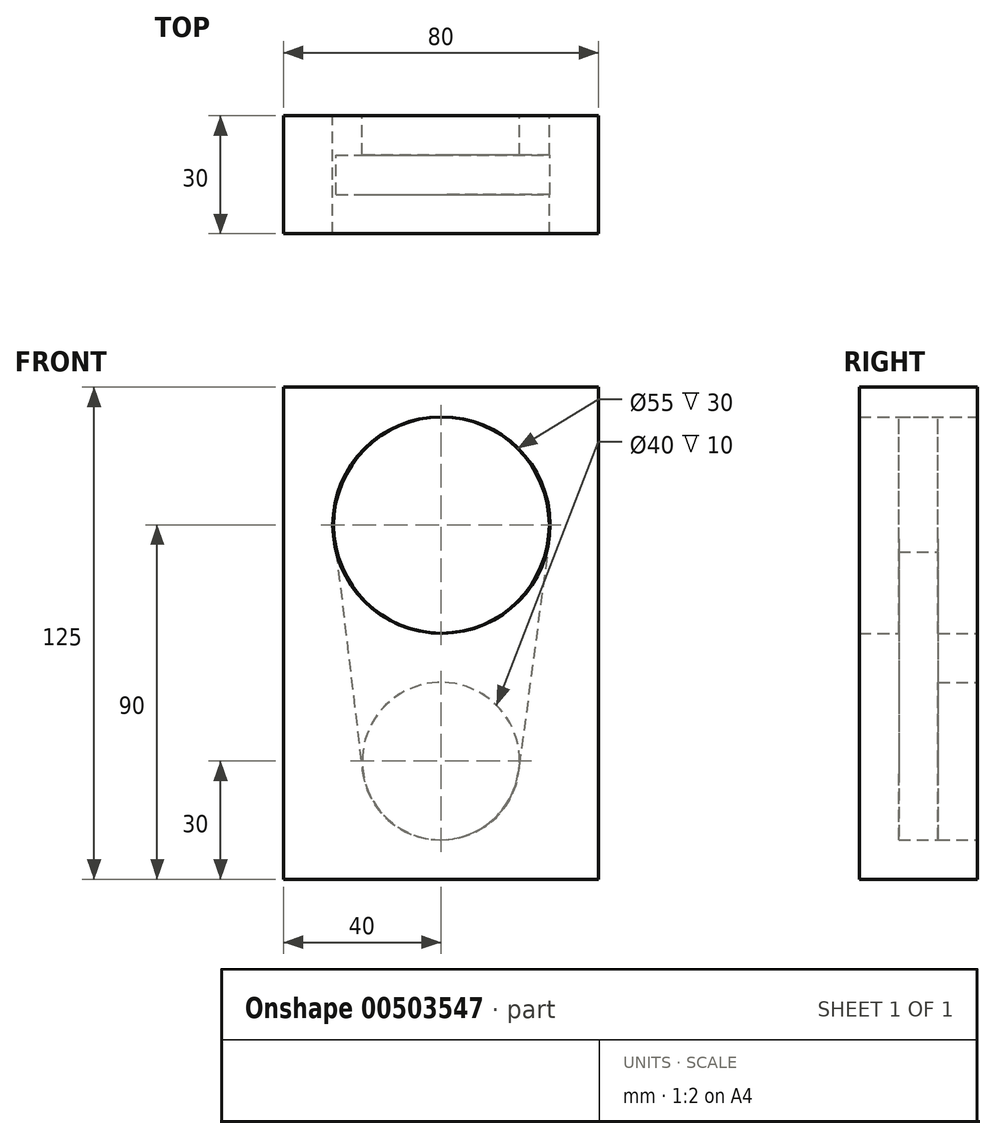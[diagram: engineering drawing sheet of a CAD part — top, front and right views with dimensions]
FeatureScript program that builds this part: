
annotation { "Feature Type Name" : "Feature", "Feature Type Description" : "" }
export const myFeature = defineFeature(function(context is Context, id is Id, definition is map)
    precondition{}
    {
        {
            var Q0;
            Q0=qCreatedBy(makeId("Front.planeOp"),FACE);
            var sketch = newSketch(context, id + "F0", { "sketchPlane" : qUnion([Q0])});
            skLineSegment(sketch, "E0", {"start": v(-27.07, 36.74) * mm, "end": v(-20, -22.37) * mm});
            skLineSegment(sketch, "E1", {"start": v(27.5, 36.4) * mm, "end": v(19.69, -22.63) * mm});
            skArc(sketch, "E2", {"start": v(-20, -22.37) * mm, "mid": v(-0.27, -40) * mm, "end": v(19.69, -22.63) * mm});
            skArc(sketch, "E3", {"start": v(27.5, 36.4) * mm, "mid": v(0.41, 67.5) * mm, "end": v(-27.07, 36.74) * mm});
            skSolve(sketch);
        }
        {
            var Q0;
            Q0=qCreatedBy(makeId("Front.planeOp"),FACE);
            var sketch = newSketch(context, id + "F1", { "sketchPlane" : qUnion([Q0])});
            skCircle(sketch, "E4", {"center": v(0, -20) * mm, "radius": 20 * mm});
            skSolve(sketch);
        }
        {
            var Q0;
            Q0=qCreatedBy(makeId("Front.planeOp"),FACE);
            var sketch = newSketch(context, id + "F2", { "sketchPlane" : qUnion([Q0])});
            skLineSegment(sketch, "E5.bottom", {"start": v(-40, 75) * mm, "end": v(40, 75) * mm});
            skLineSegment(sketch, "E5.top", {"start": v(-40, -50) * mm, "end": v(40, -50) * mm});
            skLineSegment(sketch, "E5.left", {"start": v(-40, 75) * mm, "end": v(-40, -50) * mm});
            skLineSegment(sketch, "E5.right", {"start": v(40, 75) * mm, "end": v(40, -50) * mm});
            skCircle(sketch, "E6", {"center": v(0, 40) * mm, "radius": 27.5 * mm});
            skSolve(sketch);
        }
        {
            var Q0;
            Q0 = qSketchRegion(id + "F2", true);
            extrude(context, id + "F3", {"entities" : qUnion([Q0]), "depth" : 30 * mm});
        }
        {
            var Q0;
            Q0 = qSketchRegion(id + "F0", true);
            extrude(context, id + "F4", {"entities" : qUnion([Q0]), "operationType" : NewBodyOperationType.REMOVE, "depth" : 20 * mm, "hasSecondDirection" : true, "secondDirectionOppositeDirection" : false, "secondDirectionDepth" : 10 * mm});
        }
        {
            var Q0;
            Q0 = qSketchRegion(id + "F1", true);
            extrude(context, id + "F5", {"entities" : qUnion([Q0]), "operationType" : NewBodyOperationType.REMOVE, "depth" : 10 * mm});
        }
    });
